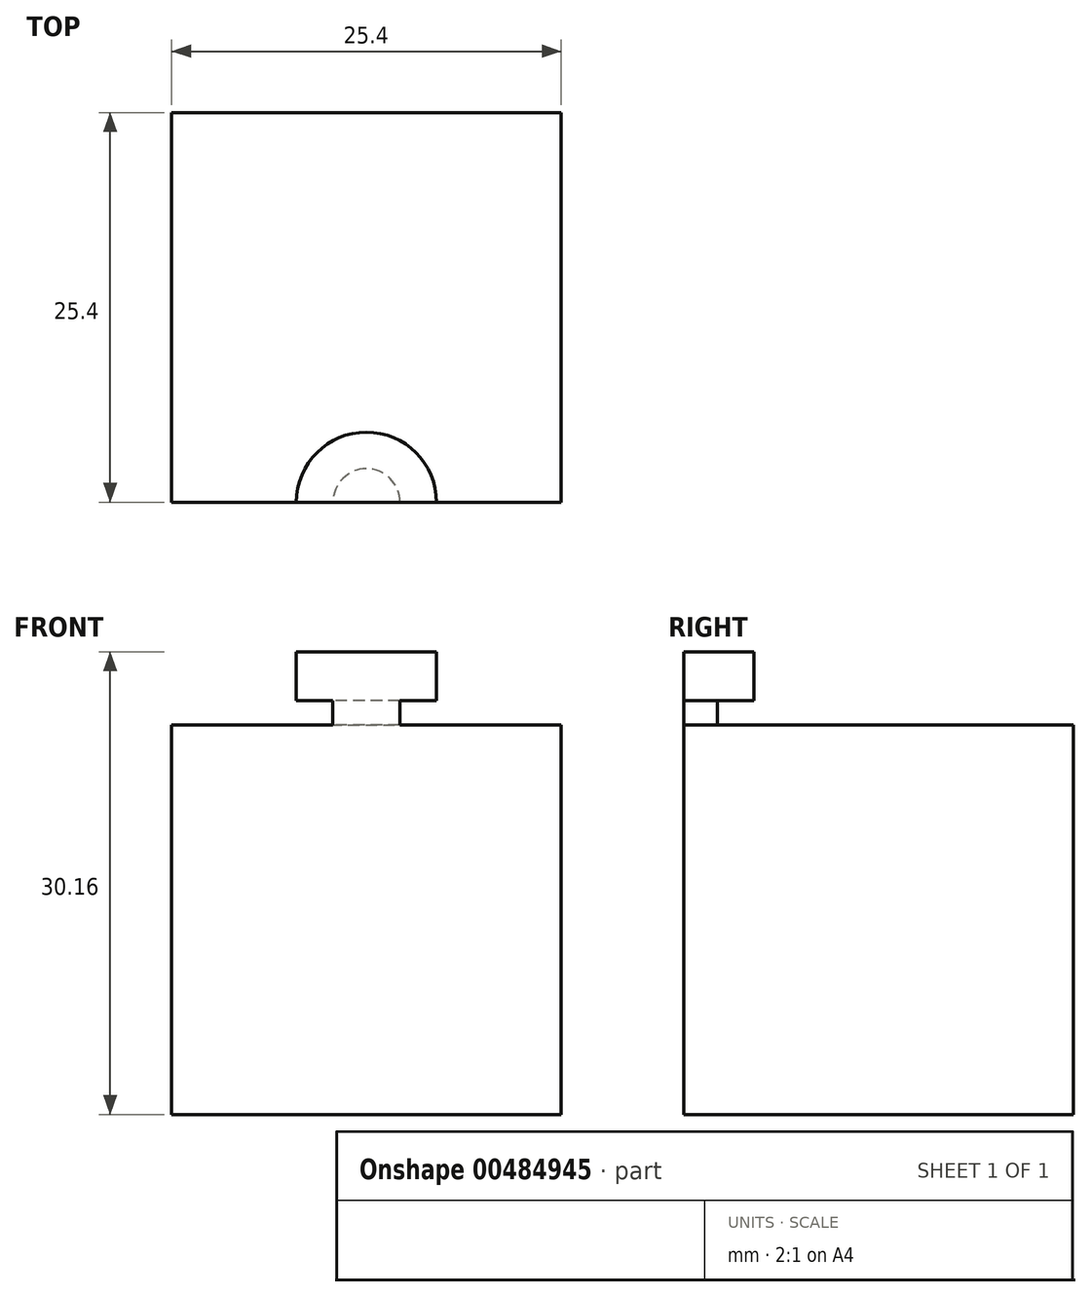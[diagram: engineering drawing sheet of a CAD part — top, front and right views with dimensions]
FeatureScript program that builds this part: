
annotation { "Feature Type Name" : "Feature", "Feature Type Description" : "" }
export const myFeature = defineFeature(function(context is Context, id is Id, definition is map)
    precondition{}
    {
        {
            var Q0;
            Q0=qCreatedBy(makeId("Top.planeOp"),FACE);
            var sketch = newSketch(context, id + "F0", { "sketchPlane" : qUnion([Q0])});
            skLineSegment(sketch, "E0.bottom", {"start": v(-12.7, 12.7) * mm, "end": v(12.7, 12.7) * mm});
            skLineSegment(sketch, "E0.top", {"start": v(-12.7, -12.7) * mm, "end": v(12.7, -12.7) * mm});
            skLineSegment(sketch, "E0.left", {"start": v(-12.7, 12.7) * mm, "end": v(-12.7, -12.7) * mm});
            skLineSegment(sketch, "E0.right", {"start": v(12.7, 12.7) * mm, "end": v(12.7, -12.7) * mm});
            skSolve(sketch);
        }
        {
            var Q0;
            Q0 = qSketchRegion(id + "F0", true);
            extrude(context, id + "F1", {"entities" : qUnion([Q0]), "depth" : 25.4 * mm});
        }
        {
            var Q0;
            Q0=makeQuery(id+"F1.opExtrude","CAP_FACE",FACE,{"disambiguationData":[OSD([sQuery(id+"F0.wireOp",EDGE,"E0.bottom"),sQuery(id+"F0.wireOp",EDGE,"E0.top"),sQuery(id+"F0.wireOp",EDGE,"E0.left"),sQuery(id+"F0.wireOp",EDGE,"E0.right")])],"isStart":false});
            var sketch = newSketch(context, id + "F2", { "sketchPlane" : qUnion([Q0])});
            skArc(sketch, "E1", {"start": v(2.18, -12.7) * mm, "mid": v(0, -10.52) * mm, "end": v(-2.18, -12.7) * mm});
            skLineSegment(sketch, "E2", {"start": v(-2.18, -12.7) * mm, "end": v(2.18, -12.7) * mm});
            skSolve(sketch);
        }
        {
            var Q0;
            Q0 = qSketchRegion(id + "F2", true);
            extrude(context, id + "F3", {"entities" : qUnion([Q0]), "operationType" : NewBodyOperationType.ADD, "depth" : 1.59 * mm});
        }
        {
            var Q0;
            Q0=makeQuery(id+"F3.opExtrude","CAP_FACE",FACE,{"disambiguationData":[OSD([sQuery(id+"F2.wireOp",EDGE,"E1")])],"isStart":false});
            var sketch = newSketch(context, id + "F4", { "sketchPlane" : qUnion([Q0])});
            skArc(sketch, "E3", {"start": v(4.56, -12.7) * mm, "mid": v(0, -8.14) * mm, "end": v(-4.56, -12.7) * mm});
            skLineSegment(sketch, "E4", {"start": v(4.56, -12.7) * mm, "end": v(-4.56, -12.7) * mm});
            skSolve(sketch);
        }
        {
            var Q0;
            Q0 = qSketchRegion(id + "F4", true);
            extrude(context, id + "F5", {"entities" : qUnion([Q0]), "operationType" : NewBodyOperationType.ADD, "depth" : 3.17 * mm});
        }
    });
